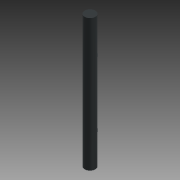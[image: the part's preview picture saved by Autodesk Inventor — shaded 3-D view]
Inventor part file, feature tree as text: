
AUTODESK INVENTOR PART (.ipt)
format: ipt  version: 2020 (Build 240168000, 168)  size: 92,672 bytes
history: native  units: mm
features: extrude x2, sketch x2, plane x1
ambient origin geometry x8: Origin, YZ Plane, XZ Plane, XY Plane, X Axis, Y Axis, Z Axis, Center Point
bodies: Solid1 (feature_tree)
feature tree (5):
  extrude  "Extrusion1"  Depth=480.0mm TaperAngle=0.0deg
  plane  "Work Plane1"
  extrude  "Extrusion2"  Depth=12.0mm
  sketch  "Sketch1"  dims[d0=38.1mm d1=480.0mm d2=0.0mm]
  sketch  "Sketch2"  dims[d4=15.0mm d5=230.0mm d6=102.0mm d8=12.0mm d9=12.0mm d11=112.0mm d12=4.011mm d13=0.0mm d14=112.0mm]
